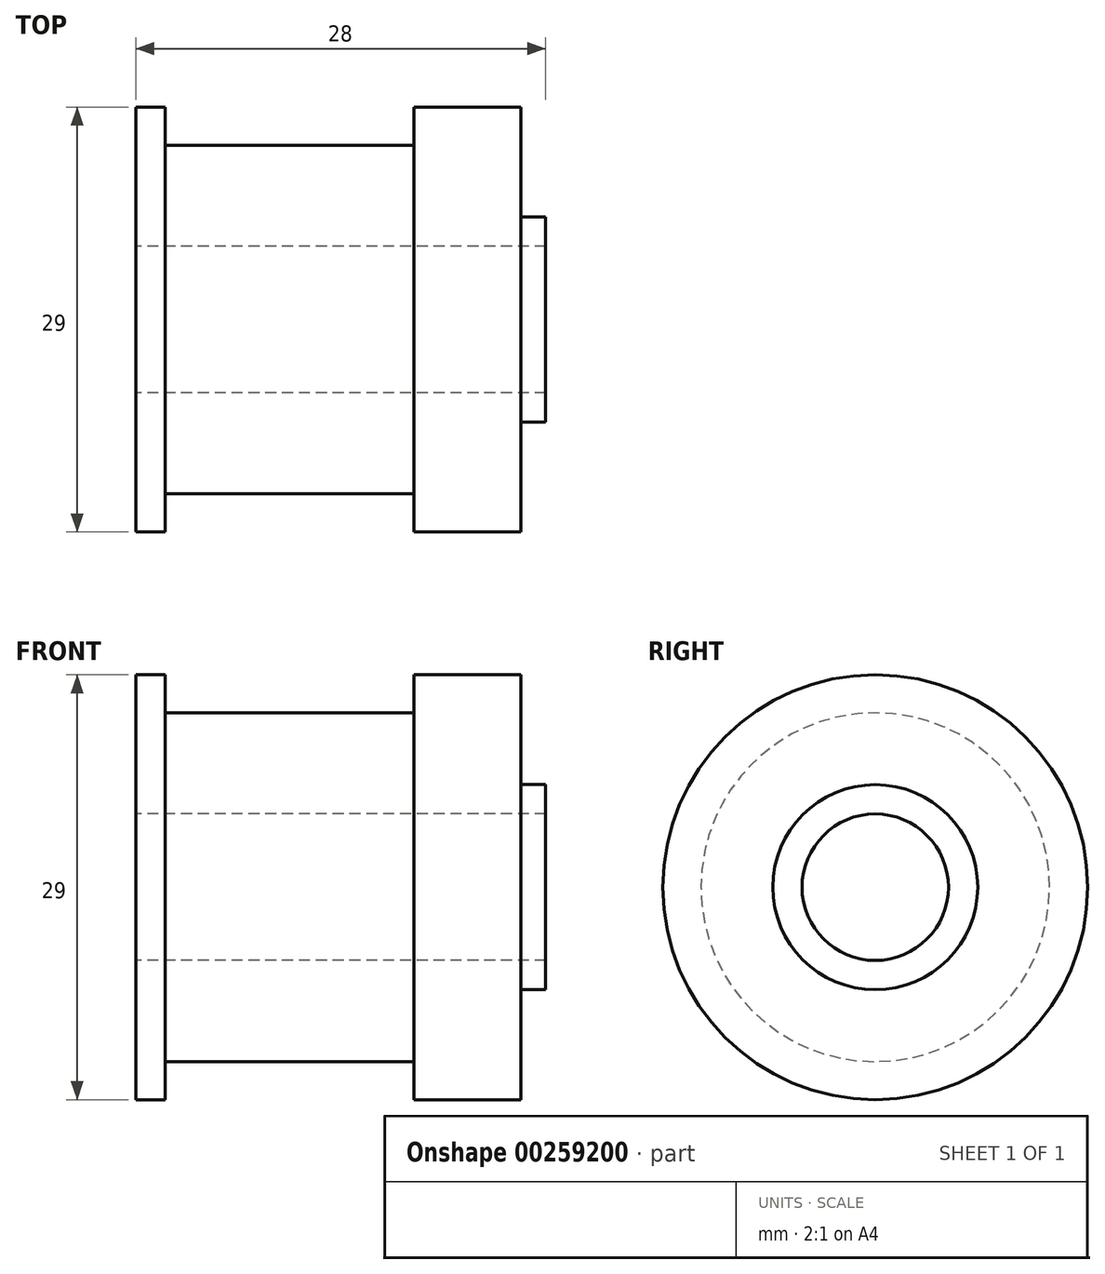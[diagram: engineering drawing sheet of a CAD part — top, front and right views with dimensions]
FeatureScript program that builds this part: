
annotation { "Feature Type Name" : "Feature", "Feature Type Description" : "" }
export const myFeature = defineFeature(function(context is Context, id is Id, definition is map)
    precondition{}
    {
        {
            var Q0;
            Q0=qCreatedBy(makeId("Front.planeOp"),FACE);
            var sketch = newSketch(context, id + "F0", { "sketchPlane" : qUnion([Q0])});
            skLineSegment(sketch, "E0", {"start": v(-9.9, 14.5) * mm, "end": v(-9.9, 5) * mm});
            skLineSegment(sketch, "E1", {"start": v(-9.9, 5) * mm, "end": v(18.1, 5) * mm});
            skLineSegment(sketch, "E2", {"start": v(16.4, 14.5) * mm, "end": v(9.1, 14.5) * mm});
            skLineSegment(sketch, "E3", {"start": v(9.1, 14.5) * mm, "end": v(9.1, 11.9) * mm});
            skLineSegment(sketch, "E4", {"start": v(9.1, 11.9) * mm, "end": v(-7.9, 11.9) * mm});
            skLineSegment(sketch, "E5", {"start": v(-7.9, 11.9) * mm, "end": v(-7.9, 14.5) * mm});
            skLineSegment(sketch, "E6", {"start": v(-7.9, 14.5) * mm, "end": v(-9.9, 14.5) * mm});
            skLineSegment(sketch, "E7", {"start": v(18.1, 5) * mm, "end": v(18.1, 7) * mm});
            skLineSegment(sketch, "E8", {"start": v(18.1, 7) * mm, "end": v(16.4, 7) * mm});
            skLineSegment(sketch, "E9", {"start": v(16.4, 7) * mm, "end": v(16.4, 14.5) * mm});
            skLineSegment(sketch, "E10", {"start": v(-14.34, 0) * mm, "end": v(22.03, 0) * mm});
            skSolve(sketch);
        }
        {
            var Q0;
            Q0 = qSketchRegion(id + "F0", true);
            var Q1;
            Q1=sQuery(id+"F0.wireOp",EDGE,"E10");
            revolve(context, id + "F1", {"entities" : qUnion([Q0]), "axis" : qUnion([Q1]), "revolveType" : RevolveType.FULL});
        }
    });
